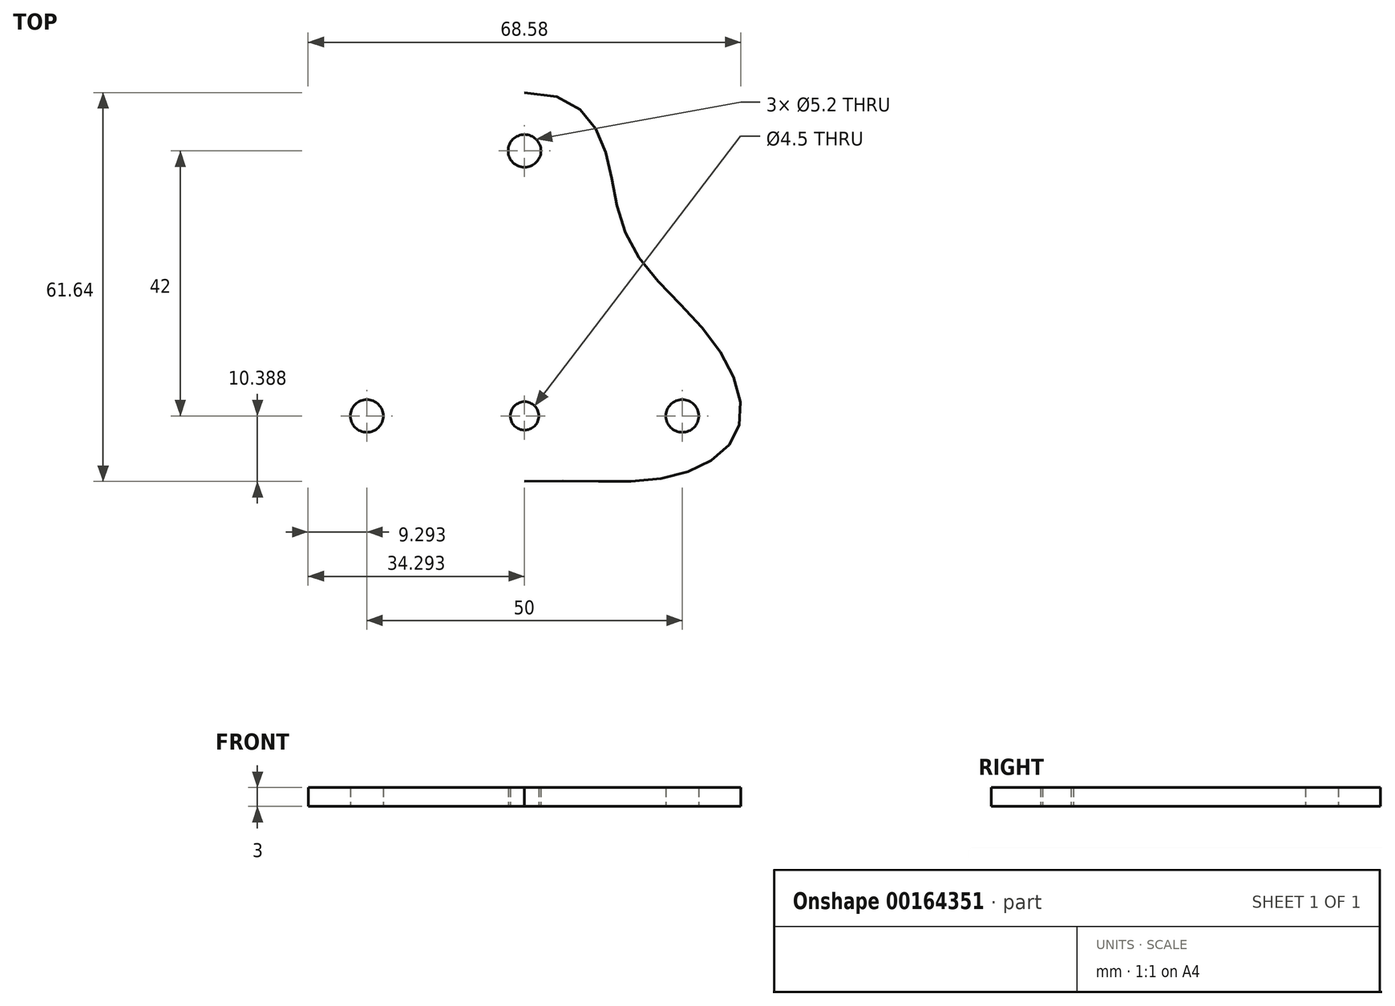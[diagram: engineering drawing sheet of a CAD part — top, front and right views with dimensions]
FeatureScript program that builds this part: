
annotation { "Feature Type Name" : "Feature", "Feature Type Description" : "" }
export const myFeature = defineFeature(function(context is Context, id is Id, definition is map)
    precondition{}
    {
        {
            var Q0;
            Q0=qCreatedBy(makeId("Top.planeOp"),FACE);
            var sketch = newSketch(context, id + "F0", { "sketchPlane" : qUnion([Q0])});
            skCircle(sketch, "E0", {"center": v(12.46, 4.43) * mm, "radius": 2.6 * mm});
            skCircle(sketch, "E1", {"center": v(37.46, -37.57) * mm, "radius": 2.6 * mm});
            skCircle(sketch, "E2", {"center": v(-12.54, -37.57) * mm, "radius": 2.6 * mm});
            skLineSegment(sketch, "E3", {"start": v(12.46, 5.9) * mm, "end": v(12.46, -52.9) * mm, "construction": true});
            skFitSpline(sketch, "E4", {"points": [v(12.46, 13.68) * mm, v(24.74, 5.9) * mm, v(29.06, -9.94) * mm, v(42.45, -25.92) * mm, v(46.34, -39.46) * mm, v(36.7, -46.95) * mm, v(12.46, -47.95) * mm], "startDerivative": vector(135.1, 3) * mm, "endDerivative": vector(-145.53, -5.3) * mm});
            skFitSpline(sketch, "E5.MirrorCS", {"points": [v(12.46, 13.68) * mm, v(0.18, 5.9) * mm, v(-4.14, -9.94) * mm, v(-17.53, -25.92) * mm, v(-21.42, -39.46) * mm, v(-11.77, -46.95) * mm, v(12.46, -47.95) * mm], "startDerivative": vector(-135.1, 3) * mm, "endDerivative": vector(145.53, -5.3) * mm});
            skCircle(sketch, "E6", {"center": v(12.46, -37.57) * mm, "radius": 2.25 * mm});
            skSolve(sketch);
        }
        {
            var Q0;
            Q0 = qSketchRegion(id + "F0", true);
            extrude(context, id + "F1", {"entities" : qUnion([Q0]), "depth" : 3 * mm});
        }
        {
            var Q0;
            Q0=makeQuery(id+"F1.opExtrude","CAP_FACE",FACE,{"disambiguationData":[OSD([sQuery(id+"F0.wireOp",EDGE,"E0"),sQuery(id+"F0.wireOp",EDGE,"E1"),sQuery(id+"F0.wireOp",EDGE,"E2"),sQuery(id+"F0.wireOp",EDGE,"dVXcSlPP-XXvO-6OeD-0uax-jvAfKnYlGIrO"),sQuery(id+"F0.wireOp",EDGE,"gXV22Ezd-BxGV-p7MN-5mEq-ep9CFymhMpRn"),sQuery(id+"F0.wireOp",EDGE,"WmkqfEUB-IWB8-ESqq-jCjN-kpA6IxgFtCK6"),sQuery(id+"F0.wireOp",EDGE,"E4"),sQuery(id+"F0.wireOp",EDGE,"E5.MirrorCS")])],"isStart":false});
            var sketch = newSketch(context, id + "F2", { "sketchPlane" : qUnion([Q0])});
            skCircle(sketch, "E7", {"center": v(13.2, -12.8) * mm, "radius": 8.8 * mm});
            skCircle(sketch, "E8", {"center": v(2.84, -28.45) * mm, "radius": 6.03 * mm});
            skCircle(sketch, "E9", {"center": v(22.14, -29.31) * mm, "radius": 6.13 * mm});
            skSolve(sketch);
        }
    });
